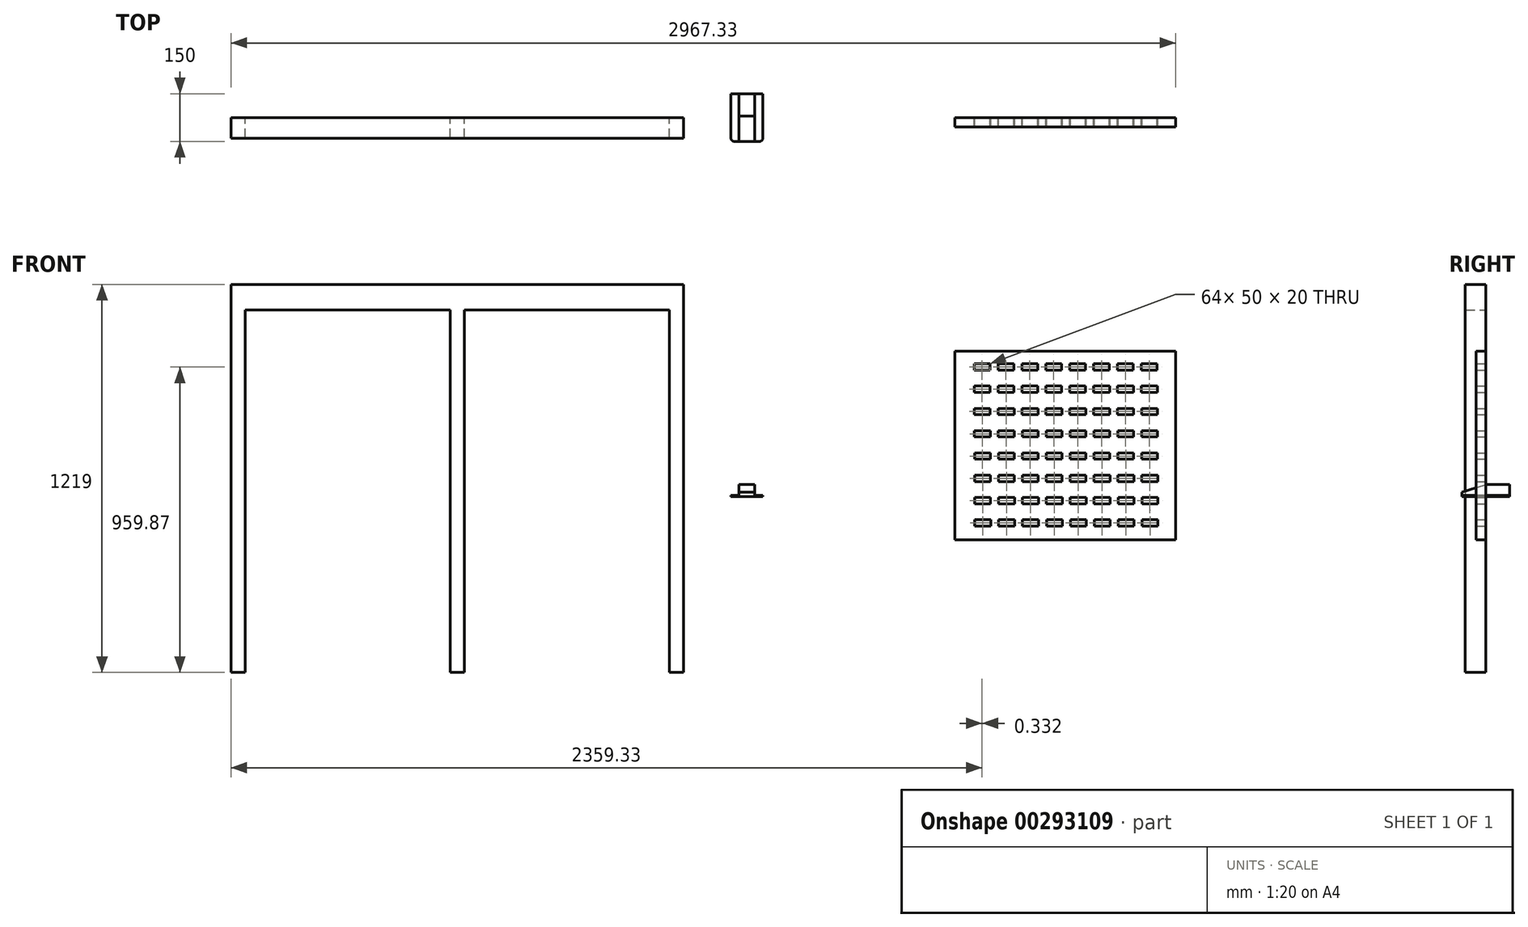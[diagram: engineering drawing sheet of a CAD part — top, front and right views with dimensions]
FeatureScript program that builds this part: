
annotation { "Feature Type Name" : "Feature", "Feature Type Description" : "" }
export const myFeature = defineFeature(function(context is Context, id is Id, definition is map)
    precondition{}
    {
        {
            var Q0;
            Q0=qCreatedBy(makeId("Top.planeOp"),FACE);
            var sketch = newSketch(context, id + "F0", { "sketchPlane" : qUnion([Q0])});
            skLineSegment(sketch, "E0.bottom", {"start": v(-50, 75) * mm, "end": v(50, 75) * mm});
            skLineSegment(sketch, "E0.top", {"start": v(-50, -75) * mm, "end": v(50, -75) * mm});
            skLineSegment(sketch, "E0.left", {"start": v(-50, 75) * mm, "end": v(-50, -75) * mm});
            skLineSegment(sketch, "E0.right", {"start": v(50, 75) * mm, "end": v(50, -75) * mm});
            skPoint(sketch, "E0.middle", {"position": v(0, 0) * mm});
            skSolve(sketch);
        }
        {
            var Q0;
            Q0=makeQuery(id+"F0.imprint","IMPRINT",FACE,{"disambiguationData":[TD([[makeQuery(id+"F0.imprint","IMPRINT",EDGE,{"derivedFrom":sQuery(id+"F0.wireOp",EDGE,"E0.bottom")}),-1.0]])]});
            extrude(context, id + "F1", {"entities" : qUnion([Q0]), "depth" : 3 * mm});
        }
        {
            var Q0;
            Q0=makeQuery(id+"F1.opExtrude","SWEPT_EDGE",EDGE,{"disambiguationData":[OSD([sQuery(id+"F0.wireOp",EDGE,"E0.top"),sQuery(id+"F0.wireOp",EDGE,"E0.left")])]});
            var Q1;
            Q1=makeQuery(id+"F1.opExtrude","SWEPT_EDGE",EDGE,{"disambiguationData":[OSD([sQuery(id+"F0.wireOp",EDGE,"E0.top"),sQuery(id+"F0.wireOp",EDGE,"E0.right")])]});
            fillet(context, id + "F2", {"entities" : qUnion([Q0, Q1]), "radius" : 10 * mm, "tangentPropagation" : true, "allowEdgeOverflow" : false});
        }
        {
            var Q0;
            Q0=makeQuery(id+"F1.opExtrude","CAP_FACE",FACE,{"disambiguationData":[OSD([sQuery(id+"F0.wireOp",EDGE,"E0.bottom"),sQuery(id+"F0.wireOp",EDGE,"E0.top"),sQuery(id+"F0.wireOp",EDGE,"E0.left"),sQuery(id+"F0.wireOp",EDGE,"E0.right")])],"isStart":false});
            var sketch = newSketch(context, id + "F3", { "sketchPlane" : qUnion([Q0])});
            skLineSegment(sketch, "E1.bottom", {"start": v(-25, 75) * mm, "end": v(25, 75) * mm});
            skLineSegment(sketch, "E1.top", {"start": v(-25, -75) * mm, "end": v(25, -75) * mm});
            skLineSegment(sketch, "E1.left", {"start": v(-25, 75) * mm, "end": v(-25, -75) * mm});
            skLineSegment(sketch, "E1.right", {"start": v(25, 75) * mm, "end": v(25, -75) * mm});
            skPoint(sketch, "E1.middle", {"position": v(0, 0) * mm});
            skSolve(sketch);
        }
        {
            var Q0;
            {var subQ0=sQuery(id+"F3.wireOp",EDGE,"E1.bottom");Q0=makeQuery(id+"F3.imprint","IMPRINT",FACE,{"disambiguationData":[TD([[makeQuery(id+"F3.imprint","IMPRINT",EDGE,{"derivedFrom":subQ0}),-1.0]])]});}
            extrude(context, id + "F4", {"entities" : qUnion([Q0]), "operationType" : NewBodyOperationType.ADD, "depth" : 35 * mm});
        }
        {
            var Q0;
            Q0=makeQuery(id+"F4.opExtrude","SWEPT_FACE",FACE,{"disambiguationData":[OSD([sQuery(id+"F3.wireOp",EDGE,"E1.right")])]});
            var sketch = newSketch(context, id + "F5", { "sketchPlane" : qUnion([Q0])});
            skLineSegment(sketch, "E2", {"start": v(5, 3) * mm, "end": v(5, 38) * mm});
            skLineSegment(sketch, "E3", {"start": v(5, 38) * mm, "end": v(-75, 13) * mm});
            skLineSegment(sketch, "E4", {"start": v(-75, 13) * mm, "end": v(-75, 3) * mm});
            skLineSegment(sketch, "E5", {"start": v(-75, 3) * mm, "end": v(5, 3) * mm});
            skSolve(sketch);
        }
        {
            var Q0;
            {var subQ0=sQuery(id+"F5.wireOp",EDGE,"E3");Q0=makeQuery(id+"F5.imprint","IMPRINT",FACE,{"disambiguationData":[TD([[makeQuery(id+"F5.imprint","IMPRINT",EDGE,{"derivedFrom":subQ0}),-1.0]])]});}
            extrude(context, id + "F6", {"entities" : qUnion([Q0]), "operationType" : NewBodyOperationType.REMOVE, "endBound" : BoundingType.THROUGH_ALL, "oppositeDirection" : true, "depth" : 25 * mm});
        }
        {
            var Q0;
            Q0=qCreatedBy(makeId("Front.planeOp"),FACE);
            var sketch = newSketch(context, id + "F7", { "sketchPlane" : qUnion([Q0])});
            skLineSegment(sketch, "E6.bottom", {"start": v(-1620.62, -552.87) * mm, "end": v(-1575.62, -552.87) * mm});
            skLineSegment(sketch, "E6.top", {"start": v(-1620.62, 666.13) * mm, "end": v(-1575.62, 666.13) * mm});
            skLineSegment(sketch, "E6.left", {"start": v(-1620.62, -552.87) * mm, "end": v(-1620.62, 666.13) * mm});
            skLineSegment(sketch, "E6.right", {"start": v(-1575.62, -552.87) * mm, "end": v(-1575.62, 666.13) * mm});
            skLineSegment(sketch, "E7.bottom", {"start": v(-1575.62, 666.13) * mm, "end": v(-932.12, 666.13) * mm});
            skLineSegment(sketch, "E7.top", {"start": v(-1575.62, 586.13) * mm, "end": v(-932.12, 586.13) * mm});
            skLineSegment(sketch, "E7.left", {"start": v(-1575.62, 666.13) * mm, "end": v(-1575.62, 586.13) * mm});
            skLineSegment(sketch, "E7.right", {"start": v(-932.12, 666.13) * mm, "end": v(-932.12, 586.13) * mm});
            skLineSegment(sketch, "E8.bottom", {"start": v(-932.12, 666.13) * mm, "end": v(-887.12, 666.13) * mm});
            skLineSegment(sketch, "E8.top", {"start": v(-932.12, -552.87) * mm, "end": v(-887.12, -552.87) * mm});
            skLineSegment(sketch, "E8.left", {"start": v(-932.12, 666.13) * mm, "end": v(-932.12, -552.87) * mm});
            skLineSegment(sketch, "E8.right", {"start": v(-887.12, 666.13) * mm, "end": v(-887.12, -552.87) * mm});
            skLineSegment(sketch, "E9.bottom", {"start": v(-887.12, 666.13) * mm, "end": v(-243.62, 666.13) * mm});
            skLineSegment(sketch, "E9.top", {"start": v(-887.12, 586.13) * mm, "end": v(-243.62, 586.13) * mm});
            skLineSegment(sketch, "E9.left", {"start": v(-887.12, 666.13) * mm, "end": v(-887.12, 586.13) * mm});
            skLineSegment(sketch, "E9.right", {"start": v(-243.62, 666.13) * mm, "end": v(-243.62, 586.13) * mm});
            skLineSegment(sketch, "E10.bottom", {"start": v(-243.62, 666.13) * mm, "end": v(-198.62, 666.13) * mm});
            skLineSegment(sketch, "E10.top", {"start": v(-243.62, -552.87) * mm, "end": v(-198.62, -552.87) * mm});
            skLineSegment(sketch, "E10.left", {"start": v(-243.62, 666.13) * mm, "end": v(-243.62, -552.87) * mm});
            skLineSegment(sketch, "E10.right", {"start": v(-198.62, 666.13) * mm, "end": v(-198.62, -552.87) * mm});
            skSolve(sketch);
        }
        {
            var Q0;
            {var subQ0=sQuery(id+"F7.wireOp",EDGE,"E7.bottom");Q0=makeQuery(id+"F7.imprint","IMPRINT",FACE,{"disambiguationData":[TD([[makeQuery(id+"F7.imprint","IMPRINT",EDGE,{"derivedFrom":subQ0}),-1.0]])]});}
            var Q1;
            Q1=makeQuery(id+"F7.imprint","IMPRINT",FACE,{"disambiguationData":[TD([[makeQuery(id+"F7.imprint","IMPRINT",EDGE,{"derivedFrom":sQuery(id+"F7.wireOp",EDGE,"E6.bottom")}),1.0]])]});
            var Q2;
            {var subQ3=sQuery(id+"F7.wireOp",EDGE,"E8.bottom");Q2=makeQuery(id+"F7.imprint","IMPRINT",FACE,{"disambiguationData":[TD([[makeQuery(id+"F7.imprint","IMPRINT",EDGE,{"derivedFrom":subQ3}),-1.0]])]});}
            var Q3;
            {var subQ0=sQuery(id+"F7.wireOp",EDGE,"E9.bottom");Q3=makeQuery(id+"F7.imprint","IMPRINT",FACE,{"disambiguationData":[TD([[makeQuery(id+"F7.imprint","IMPRINT",EDGE,{"derivedFrom":subQ0}),-1.0]])]});}
            var Q4;
            {var subQ3=sQuery(id+"F7.wireOp",EDGE,"E10.bottom");Q4=makeQuery(id+"F7.imprint","IMPRINT",FACE,{"disambiguationData":[TD([[makeQuery(id+"F7.imprint","IMPRINT",EDGE,{"derivedFrom":subQ3}),-1.0]])]});}
            extrude(context, id + "F8", {"entities" : qUnion([Q0, Q1, Q2, Q3, Q4]), "depth" : 65 * mm});
        }
        {
            var Q0;
            Q0=qCreatedBy(makeId("Front.planeOp"),FACE);
            var sketch = newSketch(context, id + "F9", { "sketchPlane" : qUnion([Q0])});
            skLineSegment(sketch, "E11.bottom", {"start": v(653.71, 457) * mm, "end": v(1346.71, 457) * mm});
            skLineSegment(sketch, "E11.top", {"start": v(653.71, -136) * mm, "end": v(1346.71, -136) * mm});
            skLineSegment(sketch, "E11.left", {"start": v(653.71, 457) * mm, "end": v(653.71, -136) * mm});
            skLineSegment(sketch, "E11.right", {"start": v(1346.71, 457) * mm, "end": v(1346.71, -136) * mm});
            skLineSegment(sketch, "E12.bottom", {"start": v(713.71, 417) * mm, "end": v(763.71, 417) * mm});
            skLineSegment(sketch, "E12.top", {"start": v(713.71, 397) * mm, "end": v(763.71, 397) * mm});
            skLineSegment(sketch, "E12.left", {"start": v(713.71, 417) * mm, "end": v(713.71, 397) * mm});
            skLineSegment(sketch, "E12.right", {"start": v(763.71, 417) * mm, "end": v(763.71, 397) * mm});
            skLineSegment(sketch, "E13.0.1.0", {"start": v(714.04, 347) * mm, "end": v(764.04, 347) * mm});
            skLineSegment(sketch, "E13.0.1.1", {"start": v(714.04, 327) * mm, "end": v(764.04, 327) * mm});
            skLineSegment(sketch, "E13.0.1.2", {"start": v(714.04, 347) * mm, "end": v(714.04, 327) * mm});
            skLineSegment(sketch, "E13.0.2.0", {"start": v(714.37, 277) * mm, "end": v(764.37, 277) * mm});
            skLineSegment(sketch, "E13.0.2.1", {"start": v(714.37, 257) * mm, "end": v(764.37, 257) * mm});
            skLineSegment(sketch, "E13.0.2.2", {"start": v(714.37, 277) * mm, "end": v(714.37, 257) * mm});
            skLineSegment(sketch, "E13.0.3.0", {"start": v(714.7, 207) * mm, "end": v(764.7, 207) * mm});
            skLineSegment(sketch, "E13.0.3.1", {"start": v(714.7, 187) * mm, "end": v(764.7, 187) * mm});
            skLineSegment(sketch, "E13.0.3.2", {"start": v(714.7, 207) * mm, "end": v(714.7, 187) * mm});
            skLineSegment(sketch, "E13.0.4.0", {"start": v(715.04, 137) * mm, "end": v(765.04, 137) * mm});
            skLineSegment(sketch, "E13.0.4.1", {"start": v(715.04, 117) * mm, "end": v(765.04, 117) * mm});
            skLineSegment(sketch, "E13.0.4.2", {"start": v(715.04, 137) * mm, "end": v(715.04, 117) * mm});
            skLineSegment(sketch, "E13.0.5.0", {"start": v(715.37, 67) * mm, "end": v(765.37, 67) * mm});
            skLineSegment(sketch, "E13.0.5.1", {"start": v(715.37, 47) * mm, "end": v(765.37, 47) * mm});
            skLineSegment(sketch, "E13.0.5.2", {"start": v(715.37, 67) * mm, "end": v(715.37, 47) * mm});
            skLineSegment(sketch, "E13.0.6.0", {"start": v(715.7, -3) * mm, "end": v(765.7, -3) * mm});
            skLineSegment(sketch, "E13.0.6.1", {"start": v(715.7, -23) * mm, "end": v(765.7, -23) * mm});
            skLineSegment(sketch, "E13.0.6.2", {"start": v(715.7, -3) * mm, "end": v(715.7, -23) * mm});
            skLineSegment(sketch, "E13.1.0.0", {"start": v(788.71, 417) * mm, "end": v(838.71, 417) * mm});
            skLineSegment(sketch, "E13.1.0.1", {"start": v(788.71, 397) * mm, "end": v(838.71, 397) * mm});
            skLineSegment(sketch, "E13.1.0.2", {"start": v(788.71, 417) * mm, "end": v(788.71, 397) * mm});
            skLineSegment(sketch, "E13.1.1.0", {"start": v(789.04, 347) * mm, "end": v(839.04, 347) * mm});
            skLineSegment(sketch, "E13.1.1.1", {"start": v(789.04, 327) * mm, "end": v(839.04, 327) * mm});
            skLineSegment(sketch, "E13.1.1.2", {"start": v(789.04, 347) * mm, "end": v(789.04, 327) * mm});
            skLineSegment(sketch, "E13.1.2.0", {"start": v(789.37, 277) * mm, "end": v(839.37, 277) * mm});
            skLineSegment(sketch, "E13.1.2.1", {"start": v(789.37, 257) * mm, "end": v(839.37, 257) * mm});
            skLineSegment(sketch, "E13.1.2.2", {"start": v(789.37, 277) * mm, "end": v(789.37, 257) * mm});
            skLineSegment(sketch, "E13.1.3.0", {"start": v(789.7, 207) * mm, "end": v(839.7, 207) * mm});
            skLineSegment(sketch, "E13.1.3.1", {"start": v(789.7, 187) * mm, "end": v(839.7, 187) * mm});
            skLineSegment(sketch, "E13.1.3.2", {"start": v(789.7, 207) * mm, "end": v(789.7, 187) * mm});
            skLineSegment(sketch, "E13.1.4.0", {"start": v(790.04, 137) * mm, "end": v(840.04, 137) * mm});
            skLineSegment(sketch, "E13.1.4.1", {"start": v(790.04, 117) * mm, "end": v(840.04, 117) * mm});
            skLineSegment(sketch, "E13.1.4.2", {"start": v(790.04, 137) * mm, "end": v(790.04, 117) * mm});
            skLineSegment(sketch, "E13.1.5.0", {"start": v(790.37, 67) * mm, "end": v(840.37, 67) * mm});
            skLineSegment(sketch, "E13.1.5.1", {"start": v(790.37, 47) * mm, "end": v(840.37, 47) * mm});
            skLineSegment(sketch, "E13.1.5.2", {"start": v(790.37, 67) * mm, "end": v(790.37, 47) * mm});
            skLineSegment(sketch, "E13.1.6.0", {"start": v(790.7, -3) * mm, "end": v(840.7, -3) * mm});
            skLineSegment(sketch, "E13.1.6.1", {"start": v(790.7, -23) * mm, "end": v(840.7, -23) * mm});
            skLineSegment(sketch, "E13.1.6.2", {"start": v(790.7, -3) * mm, "end": v(790.7, -23) * mm});
            skLineSegment(sketch, "E13.2.0.0", {"start": v(863.71, 417) * mm, "end": v(913.71, 417) * mm});
            skLineSegment(sketch, "E13.2.0.1", {"start": v(863.71, 397) * mm, "end": v(913.71, 397) * mm});
            skLineSegment(sketch, "E13.2.0.2", {"start": v(863.71, 417) * mm, "end": v(863.71, 397) * mm});
            skLineSegment(sketch, "E13.2.1.0", {"start": v(864.04, 347) * mm, "end": v(914.04, 347) * mm});
            skLineSegment(sketch, "E13.2.1.1", {"start": v(864.04, 327) * mm, "end": v(914.04, 327) * mm});
            skLineSegment(sketch, "E13.2.1.2", {"start": v(864.04, 347) * mm, "end": v(864.04, 327) * mm});
            skLineSegment(sketch, "E13.2.2.0", {"start": v(864.37, 277) * mm, "end": v(914.37, 277) * mm});
            skLineSegment(sketch, "E13.2.2.1", {"start": v(864.37, 257) * mm, "end": v(914.37, 257) * mm});
            skLineSegment(sketch, "E13.2.2.2", {"start": v(864.37, 277) * mm, "end": v(864.37, 257) * mm});
            skLineSegment(sketch, "E13.2.3.0", {"start": v(864.7, 207) * mm, "end": v(914.7, 207) * mm});
            skLineSegment(sketch, "E13.2.3.1", {"start": v(864.7, 187) * mm, "end": v(914.7, 187) * mm});
            skLineSegment(sketch, "E13.2.3.2", {"start": v(864.7, 207) * mm, "end": v(864.7, 187) * mm});
            skLineSegment(sketch, "E13.2.4.0", {"start": v(865.04, 137) * mm, "end": v(915.04, 137) * mm});
            skLineSegment(sketch, "E13.2.4.1", {"start": v(865.04, 117) * mm, "end": v(915.04, 117) * mm});
            skLineSegment(sketch, "E13.2.4.2", {"start": v(865.04, 137) * mm, "end": v(865.04, 117) * mm});
            skLineSegment(sketch, "E13.2.5.0", {"start": v(865.37, 67) * mm, "end": v(915.37, 67) * mm});
            skLineSegment(sketch, "E13.2.5.1", {"start": v(865.37, 47) * mm, "end": v(915.37, 47) * mm});
            skLineSegment(sketch, "E13.2.5.2", {"start": v(865.37, 67) * mm, "end": v(865.37, 47) * mm});
            skLineSegment(sketch, "E13.2.6.0", {"start": v(865.7, -3) * mm, "end": v(915.7, -3) * mm});
            skLineSegment(sketch, "E13.2.6.1", {"start": v(865.7, -23) * mm, "end": v(915.7, -23) * mm});
            skLineSegment(sketch, "E13.2.6.2", {"start": v(865.7, -3) * mm, "end": v(865.7, -23) * mm});
            skLineSegment(sketch, "E13.3.0.0", {"start": v(938.71, 417) * mm, "end": v(988.71, 417) * mm});
            skLineSegment(sketch, "E13.3.0.1", {"start": v(938.71, 397) * mm, "end": v(988.71, 397) * mm});
            skLineSegment(sketch, "E13.3.0.2", {"start": v(938.71, 417) * mm, "end": v(938.71, 397) * mm});
            skLineSegment(sketch, "E13.3.1.0", {"start": v(939.04, 347) * mm, "end": v(989.04, 347) * mm});
            skLineSegment(sketch, "E13.3.1.1", {"start": v(939.04, 327) * mm, "end": v(989.04, 327) * mm});
            skLineSegment(sketch, "E13.3.1.2", {"start": v(939.04, 347) * mm, "end": v(939.04, 327) * mm});
            skLineSegment(sketch, "E13.3.2.0", {"start": v(939.37, 277) * mm, "end": v(989.37, 277) * mm});
            skLineSegment(sketch, "E13.3.2.1", {"start": v(939.37, 257) * mm, "end": v(989.37, 257) * mm});
            skLineSegment(sketch, "E13.3.2.2", {"start": v(939.37, 277) * mm, "end": v(939.37, 257) * mm});
            skLineSegment(sketch, "E13.3.3.0", {"start": v(939.7, 207) * mm, "end": v(989.7, 207) * mm});
            skLineSegment(sketch, "E13.3.3.1", {"start": v(939.7, 187) * mm, "end": v(989.7, 187) * mm});
            skLineSegment(sketch, "E13.3.3.2", {"start": v(939.7, 207) * mm, "end": v(939.7, 187) * mm});
            skLineSegment(sketch, "E13.3.4.0", {"start": v(940.04, 137) * mm, "end": v(990.04, 137) * mm});
            skLineSegment(sketch, "E13.3.4.1", {"start": v(940.04, 117) * mm, "end": v(990.04, 117) * mm});
            skLineSegment(sketch, "E13.3.4.2", {"start": v(940.04, 137) * mm, "end": v(940.04, 117) * mm});
            skLineSegment(sketch, "E13.3.5.0", {"start": v(940.37, 67) * mm, "end": v(990.37, 67) * mm});
            skLineSegment(sketch, "E13.3.5.1", {"start": v(940.37, 47) * mm, "end": v(990.37, 47) * mm});
            skLineSegment(sketch, "E13.3.5.2", {"start": v(940.37, 67) * mm, "end": v(940.37, 47) * mm});
            skLineSegment(sketch, "E13.3.6.0", {"start": v(940.7, -3) * mm, "end": v(990.7, -3) * mm});
            skLineSegment(sketch, "E13.3.6.1", {"start": v(940.7, -23) * mm, "end": v(990.7, -23) * mm});
            skLineSegment(sketch, "E13.3.6.2", {"start": v(940.7, -3) * mm, "end": v(940.7, -23) * mm});
            skLineSegment(sketch, "E13.4.0.0", {"start": v(1013.71, 417) * mm, "end": v(1063.71, 417) * mm});
            skLineSegment(sketch, "E13.4.0.1", {"start": v(1013.71, 397) * mm, "end": v(1063.71, 397) * mm});
            skLineSegment(sketch, "E13.4.0.2", {"start": v(1013.71, 417) * mm, "end": v(1013.71, 397) * mm});
            skLineSegment(sketch, "E13.4.1.0", {"start": v(1014.04, 347) * mm, "end": v(1064.04, 347) * mm});
            skLineSegment(sketch, "E13.4.1.1", {"start": v(1014.04, 327) * mm, "end": v(1064.04, 327) * mm});
            skLineSegment(sketch, "E13.4.1.2", {"start": v(1014.04, 347) * mm, "end": v(1014.04, 327) * mm});
            skLineSegment(sketch, "E13.4.2.0", {"start": v(1014.37, 277) * mm, "end": v(1064.37, 277) * mm});
            skLineSegment(sketch, "E13.4.2.1", {"start": v(1014.37, 257) * mm, "end": v(1064.37, 257) * mm});
            skLineSegment(sketch, "E13.4.2.2", {"start": v(1014.37, 277) * mm, "end": v(1014.37, 257) * mm});
            skLineSegment(sketch, "E13.4.3.0", {"start": v(1014.7, 207) * mm, "end": v(1064.7, 207) * mm});
            skLineSegment(sketch, "E13.4.3.1", {"start": v(1014.7, 187) * mm, "end": v(1064.7, 187) * mm});
            skLineSegment(sketch, "E13.4.3.2", {"start": v(1014.7, 207) * mm, "end": v(1014.7, 187) * mm});
            skLineSegment(sketch, "E13.4.4.0", {"start": v(1015.04, 137) * mm, "end": v(1065.04, 137) * mm});
            skLineSegment(sketch, "E13.4.4.1", {"start": v(1015.04, 117) * mm, "end": v(1065.04, 117) * mm});
            skLineSegment(sketch, "E13.4.4.2", {"start": v(1015.04, 137) * mm, "end": v(1015.04, 117) * mm});
            skLineSegment(sketch, "E13.4.5.0", {"start": v(1015.37, 67) * mm, "end": v(1065.37, 67) * mm});
            skLineSegment(sketch, "E13.4.5.1", {"start": v(1015.37, 47) * mm, "end": v(1065.37, 47) * mm});
            skLineSegment(sketch, "E13.4.5.2", {"start": v(1015.37, 67) * mm, "end": v(1015.37, 47) * mm});
            skLineSegment(sketch, "E13.4.6.0", {"start": v(1015.7, -3) * mm, "end": v(1065.7, -3) * mm});
            skLineSegment(sketch, "E13.4.6.1", {"start": v(1015.7, -23) * mm, "end": v(1065.7, -23) * mm});
            skLineSegment(sketch, "E13.4.6.2", {"start": v(1015.7, -3) * mm, "end": v(1015.7, -23) * mm});
            skLineSegment(sketch, "E13.5.0.0", {"start": v(1088.71, 417) * mm, "end": v(1138.71, 417) * mm});
            skLineSegment(sketch, "E13.5.0.1", {"start": v(1088.71, 397) * mm, "end": v(1138.71, 397) * mm});
            skLineSegment(sketch, "E13.5.0.2", {"start": v(1088.71, 417) * mm, "end": v(1088.71, 397) * mm});
            skLineSegment(sketch, "E13.5.1.0", {"start": v(1089.04, 347) * mm, "end": v(1139.04, 347) * mm});
            skLineSegment(sketch, "E13.5.1.1", {"start": v(1089.04, 327) * mm, "end": v(1139.04, 327) * mm});
            skLineSegment(sketch, "E13.5.1.2", {"start": v(1089.04, 347) * mm, "end": v(1089.04, 327) * mm});
            skLineSegment(sketch, "E13.5.2.0", {"start": v(1089.37, 277) * mm, "end": v(1139.37, 277) * mm});
            skLineSegment(sketch, "E13.5.2.1", {"start": v(1089.37, 257) * mm, "end": v(1139.37, 257) * mm});
            skLineSegment(sketch, "E13.5.2.2", {"start": v(1089.37, 277) * mm, "end": v(1089.37, 257) * mm});
            skLineSegment(sketch, "E13.5.3.0", {"start": v(1089.7, 207) * mm, "end": v(1139.7, 207) * mm});
            skLineSegment(sketch, "E13.5.3.1", {"start": v(1089.7, 187) * mm, "end": v(1139.7, 187) * mm});
            skLineSegment(sketch, "E13.5.3.2", {"start": v(1089.7, 207) * mm, "end": v(1089.7, 187) * mm});
            skLineSegment(sketch, "E13.5.4.0", {"start": v(1090.04, 137) * mm, "end": v(1140.04, 137) * mm});
            skLineSegment(sketch, "E13.5.4.1", {"start": v(1090.04, 117) * mm, "end": v(1140.04, 117) * mm});
            skLineSegment(sketch, "E13.5.4.2", {"start": v(1090.04, 137) * mm, "end": v(1090.04, 117) * mm});
            skLineSegment(sketch, "E13.5.5.0", {"start": v(1090.37, 67) * mm, "end": v(1140.37, 67) * mm});
            skLineSegment(sketch, "E13.5.5.1", {"start": v(1090.37, 47) * mm, "end": v(1140.37, 47) * mm});
            skLineSegment(sketch, "E13.5.5.2", {"start": v(1090.37, 67) * mm, "end": v(1090.37, 47) * mm});
            skLineSegment(sketch, "E13.5.6.0", {"start": v(1090.7, -3) * mm, "end": v(1140.7, -3) * mm});
            skLineSegment(sketch, "E13.5.6.1", {"start": v(1090.7, -23) * mm, "end": v(1140.7, -23) * mm});
            skLineSegment(sketch, "E13.5.6.2", {"start": v(1090.7, -3) * mm, "end": v(1090.7, -23) * mm});
            skLineSegment(sketch, "E13.6.0.0", {"start": v(1163.71, 417) * mm, "end": v(1213.71, 417) * mm});
            skLineSegment(sketch, "E13.6.0.1", {"start": v(1163.71, 397) * mm, "end": v(1213.71, 397) * mm});
            skLineSegment(sketch, "E13.6.0.2", {"start": v(1163.71, 417) * mm, "end": v(1163.71, 397) * mm});
            skLineSegment(sketch, "E13.6.1.0", {"start": v(1164.04, 347) * mm, "end": v(1214.04, 347) * mm});
            skLineSegment(sketch, "E13.6.1.1", {"start": v(1164.04, 327) * mm, "end": v(1214.04, 327) * mm});
            skLineSegment(sketch, "E13.6.1.2", {"start": v(1164.04, 347) * mm, "end": v(1164.04, 327) * mm});
            skLineSegment(sketch, "E13.6.2.0", {"start": v(1164.37, 277) * mm, "end": v(1214.37, 277) * mm});
            skLineSegment(sketch, "E13.6.2.1", {"start": v(1164.37, 257) * mm, "end": v(1214.37, 257) * mm});
            skLineSegment(sketch, "E13.6.2.2", {"start": v(1164.37, 277) * mm, "end": v(1164.37, 257) * mm});
            skLineSegment(sketch, "E13.6.3.0", {"start": v(1164.7, 207) * mm, "end": v(1214.7, 207) * mm});
            skLineSegment(sketch, "E13.6.3.1", {"start": v(1164.7, 187) * mm, "end": v(1214.7, 187) * mm});
            skLineSegment(sketch, "E13.6.3.2", {"start": v(1164.7, 207) * mm, "end": v(1164.7, 187) * mm});
            skLineSegment(sketch, "E13.6.4.0", {"start": v(1165.04, 137) * mm, "end": v(1215.04, 137) * mm});
            skLineSegment(sketch, "E13.6.4.1", {"start": v(1165.04, 117) * mm, "end": v(1215.04, 117) * mm});
            skLineSegment(sketch, "E13.6.4.2", {"start": v(1165.04, 137) * mm, "end": v(1165.04, 117) * mm});
            skLineSegment(sketch, "E13.6.5.0", {"start": v(1165.37, 67) * mm, "end": v(1215.37, 67) * mm});
            skLineSegment(sketch, "E13.6.5.1", {"start": v(1165.37, 47) * mm, "end": v(1215.37, 47) * mm});
            skLineSegment(sketch, "E13.6.5.2", {"start": v(1165.37, 67) * mm, "end": v(1165.37, 47) * mm});
            skLineSegment(sketch, "E13.6.6.0", {"start": v(1165.7, -3) * mm, "end": v(1215.7, -3) * mm});
            skLineSegment(sketch, "E13.6.6.1", {"start": v(1165.7, -23) * mm, "end": v(1215.7, -23) * mm});
            skLineSegment(sketch, "E13.6.6.2", {"start": v(1165.7, -3) * mm, "end": v(1165.7, -23) * mm});
            skLineSegment(sketch, "E13.7.0.0", {"start": v(1238.71, 417) * mm, "end": v(1288.71, 417) * mm});
            skLineSegment(sketch, "E13.7.0.1", {"start": v(1238.71, 397) * mm, "end": v(1288.71, 397) * mm});
            skLineSegment(sketch, "E13.7.0.2", {"start": v(1238.71, 417) * mm, "end": v(1238.71, 397) * mm});
            skLineSegment(sketch, "E13.7.1.0", {"start": v(1239.04, 347) * mm, "end": v(1289.04, 347) * mm});
            skLineSegment(sketch, "E13.7.1.1", {"start": v(1239.04, 327) * mm, "end": v(1289.04, 327) * mm});
            skLineSegment(sketch, "E13.7.1.2", {"start": v(1239.04, 347) * mm, "end": v(1239.04, 327) * mm});
            skLineSegment(sketch, "E13.7.2.0", {"start": v(1239.37, 277) * mm, "end": v(1289.37, 277) * mm});
            skLineSegment(sketch, "E13.7.2.1", {"start": v(1239.37, 257) * mm, "end": v(1289.37, 257) * mm});
            skLineSegment(sketch, "E13.7.2.2", {"start": v(1239.37, 277) * mm, "end": v(1239.37, 257) * mm});
            skLineSegment(sketch, "E13.7.3.0", {"start": v(1239.7, 207) * mm, "end": v(1289.7, 207) * mm});
            skLineSegment(sketch, "E13.7.3.1", {"start": v(1239.7, 187) * mm, "end": v(1289.7, 187) * mm});
            skLineSegment(sketch, "E13.7.3.2", {"start": v(1239.7, 207) * mm, "end": v(1239.7, 187) * mm});
            skLineSegment(sketch, "E13.7.4.0", {"start": v(1240.04, 137) * mm, "end": v(1290.04, 137) * mm});
            skLineSegment(sketch, "E13.7.4.1", {"start": v(1240.04, 117) * mm, "end": v(1290.04, 117) * mm});
            skLineSegment(sketch, "E13.7.4.2", {"start": v(1240.04, 137) * mm, "end": v(1240.04, 117) * mm});
            skLineSegment(sketch, "E13.7.5.0", {"start": v(1240.37, 67) * mm, "end": v(1290.37, 67) * mm});
            skLineSegment(sketch, "E13.7.5.1", {"start": v(1240.37, 47) * mm, "end": v(1290.37, 47) * mm});
            skLineSegment(sketch, "E13.7.5.2", {"start": v(1240.37, 67) * mm, "end": v(1240.37, 47) * mm});
            skLineSegment(sketch, "E13.7.6.0", {"start": v(1240.7, -3) * mm, "end": v(1290.7, -3) * mm});
            skLineSegment(sketch, "E13.7.6.1", {"start": v(1240.7, -23) * mm, "end": v(1290.7, -23) * mm});
            skLineSegment(sketch, "E13.7.6.2", {"start": v(1240.7, -3) * mm, "end": v(1240.7, -23) * mm});
            skLineSegment(sketch, "E13.direction1", {"start": v(713.71, 417) * mm, "end": v(788.71, 417) * mm, "construction": true});
            skLineSegment(sketch, "E13.direction2", {"start": v(713.71, 417) * mm, "end": v(714.04, 347) * mm, "construction": true});
            skLineSegment(sketch, "E14.0.0.7", {"start": v(716.03, -73) * mm, "end": v(766.03, -73) * mm});
            skLineSegment(sketch, "E14.3.0.7", {"start": v(716.03, -93) * mm, "end": v(766.03, -93) * mm});
            skLineSegment(sketch, "E14.6.0.7", {"start": v(716.03, -73) * mm, "end": v(716.03, -93) * mm});
            skLineSegment(sketch, "E14.0.1.7", {"start": v(791.03, -73) * mm, "end": v(841.03, -73) * mm});
            skLineSegment(sketch, "E14.3.1.7", {"start": v(791.03, -93) * mm, "end": v(841.03, -93) * mm});
            skLineSegment(sketch, "E14.6.1.7", {"start": v(791.03, -73) * mm, "end": v(791.03, -93) * mm});
            skLineSegment(sketch, "E14.0.2.7", {"start": v(866.03, -73) * mm, "end": v(916.03, -73) * mm});
            skLineSegment(sketch, "E14.3.2.7", {"start": v(866.03, -93) * mm, "end": v(916.03, -93) * mm});
            skLineSegment(sketch, "E14.6.2.7", {"start": v(866.03, -73) * mm, "end": v(866.03, -93) * mm});
            skLineSegment(sketch, "E14.0.3.7", {"start": v(941.03, -73) * mm, "end": v(991.03, -73) * mm});
            skLineSegment(sketch, "E14.3.3.7", {"start": v(941.03, -93) * mm, "end": v(991.03, -93) * mm});
            skLineSegment(sketch, "E14.6.3.7", {"start": v(941.03, -73) * mm, "end": v(941.03, -93) * mm});
            skLineSegment(sketch, "E14.0.4.7", {"start": v(1016.03, -73) * mm, "end": v(1066.03, -73) * mm});
            skLineSegment(sketch, "E14.3.4.7", {"start": v(1016.03, -93) * mm, "end": v(1066.03, -93) * mm});
            skLineSegment(sketch, "E14.6.4.7", {"start": v(1016.03, -73) * mm, "end": v(1016.03, -93) * mm});
            skLineSegment(sketch, "E14.0.5.7", {"start": v(1091.03, -73) * mm, "end": v(1141.03, -73) * mm});
            skLineSegment(sketch, "E14.3.5.7", {"start": v(1091.03, -93) * mm, "end": v(1141.03, -93) * mm});
            skLineSegment(sketch, "E14.6.5.7", {"start": v(1091.03, -73) * mm, "end": v(1091.03, -93) * mm});
            skLineSegment(sketch, "E14.0.6.7", {"start": v(1166.03, -73) * mm, "end": v(1216.03, -73) * mm});
            skLineSegment(sketch, "E14.3.6.7", {"start": v(1166.03, -93) * mm, "end": v(1216.03, -93) * mm});
            skLineSegment(sketch, "E14.6.6.7", {"start": v(1166.03, -73) * mm, "end": v(1166.03, -93) * mm});
            skLineSegment(sketch, "E14.0.7.7", {"start": v(1241.03, -73) * mm, "end": v(1291.03, -73) * mm});
            skLineSegment(sketch, "E14.3.7.7", {"start": v(1241.03, -93) * mm, "end": v(1291.03, -93) * mm});
            skLineSegment(sketch, "E14.6.7.7", {"start": v(1241.03, -73) * mm, "end": v(1241.03, -93) * mm});
            skLineSegment(sketch, "E15", {"start": v(838.71, 417) * mm, "end": v(838.71, 397) * mm});
            skLineSegment(sketch, "E16", {"start": v(913.71, 417) * mm, "end": v(913.71, 397) * mm});
            skLineSegment(sketch, "E17", {"start": v(988.71, 417) * mm, "end": v(988.71, 397) * mm});
            skLineSegment(sketch, "E18", {"start": v(1063.71, 417) * mm, "end": v(1063.71, 397) * mm});
            skLineSegment(sketch, "E19", {"start": v(1138.71, 417) * mm, "end": v(1138.71, 397) * mm});
            skLineSegment(sketch, "E20", {"start": v(1213.71, 417) * mm, "end": v(1213.71, 397) * mm});
            skLineSegment(sketch, "E21", {"start": v(1288.71, 417) * mm, "end": v(1288.71, 397) * mm});
            skLineSegment(sketch, "E22", {"start": v(1289.04, 347) * mm, "end": v(1289.04, 327) * mm});
            skLineSegment(sketch, "E23", {"start": v(1214.04, 347) * mm, "end": v(1214.04, 327) * mm});
            skLineSegment(sketch, "E24", {"start": v(1139.04, 347) * mm, "end": v(1139.04, 327) * mm});
            skLineSegment(sketch, "E25", {"start": v(1064.04, 347) * mm, "end": v(1064.04, 327) * mm});
            skLineSegment(sketch, "E26", {"start": v(989.04, 347) * mm, "end": v(989.04, 327) * mm});
            skLineSegment(sketch, "E27", {"start": v(914.04, 347) * mm, "end": v(914.04, 327) * mm});
            skLineSegment(sketch, "E28", {"start": v(839.04, 347) * mm, "end": v(839.04, 327) * mm});
            skLineSegment(sketch, "E29", {"start": v(764.04, 347) * mm, "end": v(764.04, 327) * mm});
            skLineSegment(sketch, "E30", {"start": v(764.37, 277) * mm, "end": v(764.37, 257) * mm});
            skLineSegment(sketch, "E31", {"start": v(839.37, 277) * mm, "end": v(839.37, 257) * mm});
            skLineSegment(sketch, "E32", {"start": v(914.37, 277) * mm, "end": v(914.37, 257) * mm});
            skLineSegment(sketch, "E33", {"start": v(989.37, 277) * mm, "end": v(989.37, 257) * mm});
            skLineSegment(sketch, "E34", {"start": v(1064.37, 277) * mm, "end": v(1064.37, 257) * mm});
            skLineSegment(sketch, "E35", {"start": v(1139.37, 277) * mm, "end": v(1139.37, 257) * mm});
            skLineSegment(sketch, "E36", {"start": v(1214.37, 277) * mm, "end": v(1214.37, 257) * mm});
            skLineSegment(sketch, "E37", {"start": v(1289.37, 277) * mm, "end": v(1289.37, 257) * mm});
            skLineSegment(sketch, "E38", {"start": v(1289.7, 207) * mm, "end": v(1289.7, 187) * mm});
            skLineSegment(sketch, "E39", {"start": v(1214.7, 207) * mm, "end": v(1214.7, 187) * mm});
            skLineSegment(sketch, "E40", {"start": v(1139.7, 207) * mm, "end": v(1139.7, 187) * mm});
            skLineSegment(sketch, "E41", {"start": v(1064.7, 207) * mm, "end": v(1064.7, 187) * mm});
            skLineSegment(sketch, "E42", {"start": v(989.7, 207) * mm, "end": v(989.7, 187) * mm});
            skLineSegment(sketch, "E43", {"start": v(914.7, 207) * mm, "end": v(914.7, 187) * mm});
            skLineSegment(sketch, "E44", {"start": v(839.7, 207) * mm, "end": v(839.7, 187) * mm});
            skLineSegment(sketch, "E45", {"start": v(764.7, 207) * mm, "end": v(764.7, 187) * mm});
            skLineSegment(sketch, "E46", {"start": v(765.04, 137) * mm, "end": v(765.04, 117) * mm});
            skLineSegment(sketch, "E47", {"start": v(840.04, 137) * mm, "end": v(840.04, 117) * mm});
            skLineSegment(sketch, "E48", {"start": v(915.04, 137) * mm, "end": v(915.04, 117) * mm});
            skLineSegment(sketch, "E49", {"start": v(990.04, 137) * mm, "end": v(990.04, 117) * mm});
            skLineSegment(sketch, "E50", {"start": v(1065.04, 137) * mm, "end": v(1065.04, 117) * mm});
            skLineSegment(sketch, "E51", {"start": v(1140.04, 137) * mm, "end": v(1140.04, 117) * mm});
            skLineSegment(sketch, "E52", {"start": v(1215.04, 137) * mm, "end": v(1215.04, 117) * mm});
            skLineSegment(sketch, "E53", {"start": v(1290.04, 137) * mm, "end": v(1290.04, 117) * mm});
            skLineSegment(sketch, "E54", {"start": v(1290.37, 67) * mm, "end": v(1290.37, 47) * mm});
            skLineSegment(sketch, "E55", {"start": v(1215.37, 67) * mm, "end": v(1215.37, 47) * mm});
            skLineSegment(sketch, "E56", {"start": v(1140.37, 67) * mm, "end": v(1140.37, 47) * mm});
            skLineSegment(sketch, "E57", {"start": v(1065.37, 67) * mm, "end": v(1065.37, 47) * mm});
            skLineSegment(sketch, "E58", {"start": v(990.37, 67) * mm, "end": v(990.37, 47) * mm});
            skLineSegment(sketch, "E59", {"start": v(915.37, 67) * mm, "end": v(915.37, 47) * mm});
            skLineSegment(sketch, "E60", {"start": v(840.37, 67) * mm, "end": v(840.37, 47) * mm});
            skLineSegment(sketch, "E61", {"start": v(765.37, 67) * mm, "end": v(765.37, 47) * mm});
            skLineSegment(sketch, "E62", {"start": v(765.7, -3) * mm, "end": v(765.7, -23) * mm});
            skLineSegment(sketch, "E63", {"start": v(840.7, -3) * mm, "end": v(840.7, -23) * mm});
            skLineSegment(sketch, "E64", {"start": v(915.7, -3) * mm, "end": v(915.7, -23) * mm});
            skLineSegment(sketch, "E65", {"start": v(990.7, -3) * mm, "end": v(990.7, -23) * mm});
            skLineSegment(sketch, "E66", {"start": v(1065.7, -3) * mm, "end": v(1065.7, -23) * mm});
            skLineSegment(sketch, "E67", {"start": v(1140.7, -3) * mm, "end": v(1140.7, -23) * mm});
            skLineSegment(sketch, "E68", {"start": v(1215.7, -3) * mm, "end": v(1215.7, -23) * mm});
            skLineSegment(sketch, "E69", {"start": v(1290.7, -3) * mm, "end": v(1290.7, -23) * mm});
            skLineSegment(sketch, "E70", {"start": v(1291.03, -73) * mm, "end": v(1291.03, -93) * mm});
            skLineSegment(sketch, "E71", {"start": v(1216.03, -73) * mm, "end": v(1216.03, -93) * mm});
            skLineSegment(sketch, "E72", {"start": v(1141.03, -73) * mm, "end": v(1141.03, -93) * mm});
            skLineSegment(sketch, "E73", {"start": v(1066.03, -73) * mm, "end": v(1066.03, -93) * mm});
            skLineSegment(sketch, "E74", {"start": v(991.03, -73) * mm, "end": v(991.03, -93) * mm});
            skLineSegment(sketch, "E75", {"start": v(841.03, -73) * mm, "end": v(841.03, -93) * mm});
            skLineSegment(sketch, "E76", {"start": v(766.03, -73) * mm, "end": v(766.03, -93) * mm});
            skLineSegment(sketch, "E77", {"start": v(916.03, -73) * mm, "end": v(916.03, -93) * mm});
            skSolve(sketch);
        }
        {
            var Q0;
            Q0=makeQuery(id+"F9.imprint","IMPRINT",FACE,{"disambiguationData":[TD([[makeQuery(id+"F9.imprint","IMPRINT",EDGE,{"derivedFrom":sQuery(id+"F9.wireOp",EDGE,"E11.bottom")}),-1.0]])]});
            extrude(context, id + "F10", {"entities" : qUnion([Q0]), "depth" : 30 * mm});
        }
    });
